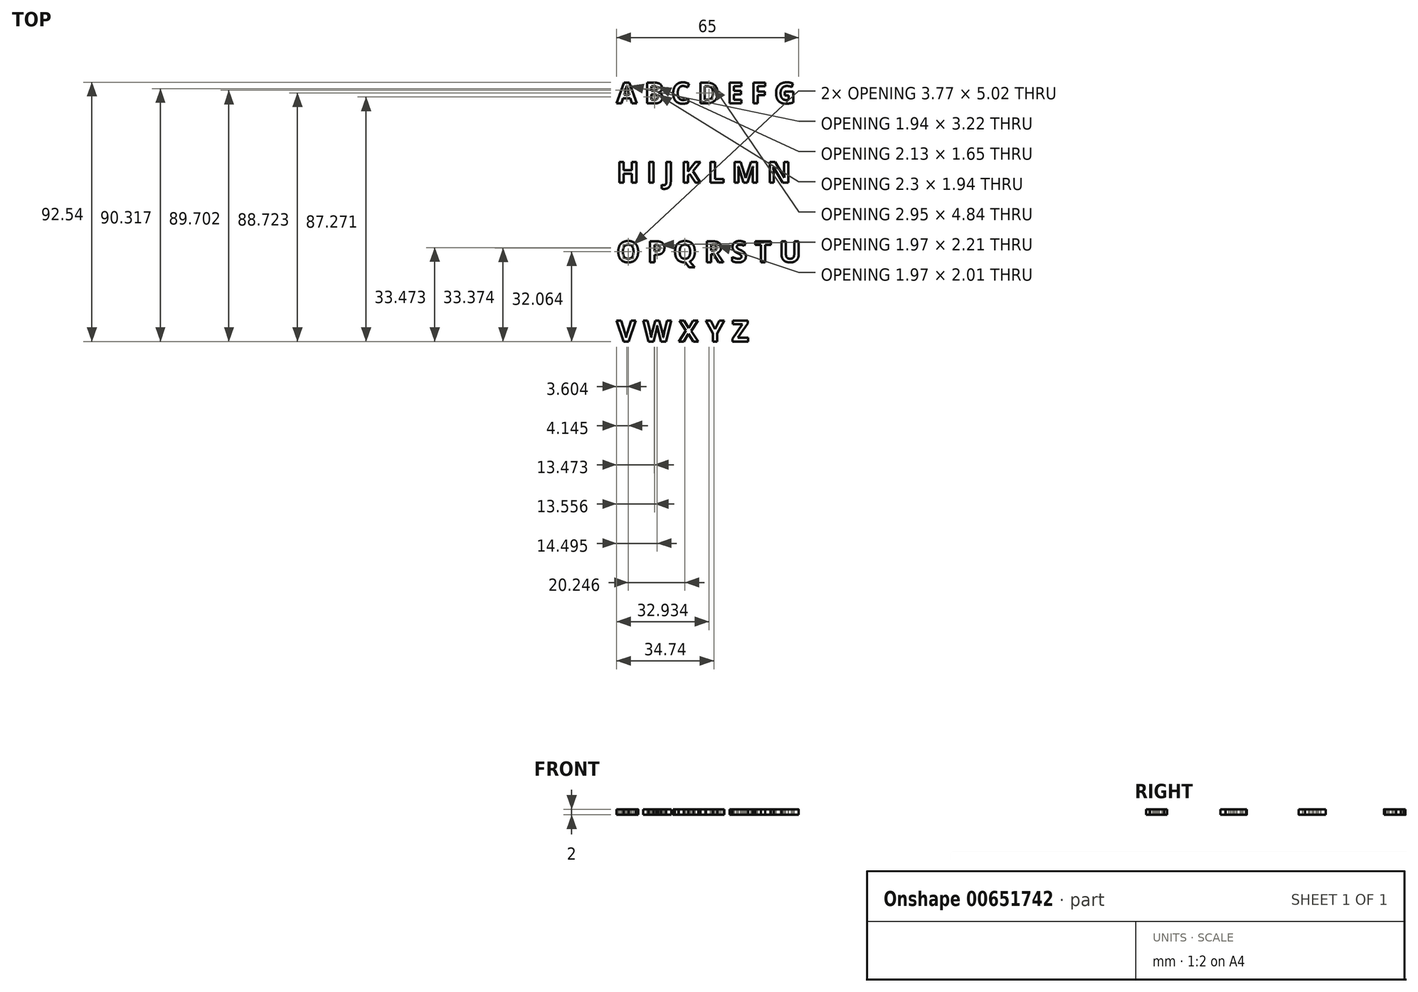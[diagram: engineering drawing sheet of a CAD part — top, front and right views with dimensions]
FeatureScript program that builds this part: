
annotation { "Feature Type Name" : "Feature", "Feature Type Description" : "" }
export const myFeature = defineFeature(function(context is Context, id is Id, definition is map)
    precondition{}
    {
        {
            var Q0;
            Q0=qCreatedBy(makeId("Top.planeOp"),FACE);
            var sketch = newSketch(context, id + "F0", { "sketchPlane" : qUnion([Q0])});
            skText(sketch, "E0", { "text": "A B C D E F G \n\nH I J K L M N\n\nO P Q R S T U\n\nV W X Y Z ", "fontName": "OpenSans-Bold.ttf"});
            const initialGuessF0  = {"E0": [-0.06653, 0.03, 1, 0, 0.0075]};
            skSetInitialGuess(sketch, initialGuessF0);
            skSolve(sketch);
        }
        {
            var Q0;
            Q0=qSketchRegion(id+"F0",true);
            extrude(context, id + "F1", {"entities" : qUnion([Q0]), "oppositeDirection" : true, "depth" : 2 * mm, "offsetDistance" : 25 * mm});
        }
    });
